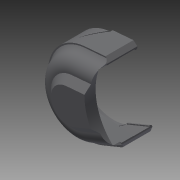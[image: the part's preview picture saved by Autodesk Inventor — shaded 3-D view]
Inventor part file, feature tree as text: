
AUTODESK INVENTOR PART (.ipt)
format: ipt  version: 2015 SP1 (Build 190203100, 203)  size: 533,504 bytes
history: native  units: in
note: dims shown in document units (in); Inventor stores cm internally (conversion verified against a paired STEP export)
features: sketch x14, projected_geometry x13, extrude x11, fillet x7, chamfer x5, plane x2, mirror x2, other x1
ambient origin geometry x8: Origin, YZ Plane, XZ Plane, XY Plane, X Axis, Y Axis, Z Axis, Center Point
bodies: Solid1 (feature_tree)
feature tree (55):
  other  "mount_sketch_alt.ipt"
  extrude  "Extrusion1"  Depth=0.3937in
  extrude  "Extrusion2"  Depth=0.625in
  extrude  "Extrusion8"  Depth=0.1575in
  extrude  "Extrusion3"  Depth=3.2677in
  chamfer  "Chamfer2"  Distance=0.1575in
  chamfer  "Chamfer5"  Distance=0.125in Angle=45.0deg
  fillet  "Fillet5"  Radius=0.0197in
  extrude  "Extrusion5"  Depth=0.125in TaperAngle=0.0deg
  extrude  "Extrusion6"  Depth=0.0197in TaperAngle=0.0deg
  extrude  "Extrusion21"  Depth=0.0295in
  extrude  "Extrusion22"  Depth=0.0295in
  chamfer  "Chamfer17"  Distance=0.0787in
  fillet  "Fillet25"  Radius=0.0394in
  fillet  "Fillet26"  Radius=0.5906in
  plane  "Work Plane6"
  mirror  "Mirror4"
  sketch  "Sketch23"  dims[d165=0.2749in d166=0.0295in]
  plane  "Work Plane5"
  extrude  "Extrusion25"  Depth=0.0394in TaperAngle=0.0deg
  chamfer  "Chamfer19"  Distance=0.0039in
  fillet  "Fillet29"  Radius=0.1969in
  fillet  "Fillet30"  Radius=0.3937in
  extrude  "Extrusion26"  Depth=0.3937in
  mirror  "Mirror6"
  extrude  "Extrusion27"  Depth=0.125in
  sketch  "Sketch28"  dims[d172=0.0197in d173=0.0394in d174=45.0deg d176=0.0394in d177=0.5906in]
  fillet  "Fillet31"  Radius=0.1969in
  chamfer  "Chamfer20"  Distance=0.0394in
  fillet  "Fillet32"  Radius=0.0394in
  sketch  "Sketch2"  dims[d0=0.3937in d1=2.507in]
  sketch  "Sketch3"  dims[d2=0.9398in d6=0.625in]
  sketch  "Sketch4"  dims[d7=0.6in d8=0.0in d9=0.1575in]
  projected_geometry  "Projected Loop1"
  sketch  "Sketch5"  dims[d10=0.52in d11=0.3in d12=0.0in d13=0.0in d18=3.2677in]
  projected_geometry  "Projected Loop2"
  sketch  "Sketch7"  dims[d19=0.9in]
  projected_geometry  "Projected Loop4"
  sketch  "Sketch8"  dims[d20=0.0394in]
  sketch  "Sketch10"  dims[d22=0.0in d23=0.1575in d24=0.0in d25=0.1181in d26=0.125in d27=45.0deg d44=0.0197in]
  projected_geometry  "Projected Loop6"
  sketch  "Sketch21"  dims[d45=0.1181in d46=0.125in d47=45.0deg d57=0.1in d58=0.0in]
  projected_geometry  "Projected Loop21"
  projected_geometry  "Projected Loop22"
  projected_geometry  "Projected Loop23"
  sketch  "Sketch22"  dims[d59=0.1in d60=0.0in d89=0.0197in d90=0.0in]
  projected_geometry  "Projected Loop24"
  projected_geometry  "Projected Loop28"
  sketch  "Sketch27"  dims[d167=0.315in d168=0.0in d169=0.0295in d170=0.0787in d171=0.0in]
  projected_geometry  "Projected Loop29"
  sketch  "Sketch30"  dims[d198=3.5827in d199=0.0394in d200=0.0in]
  projected_geometry  "Projected Loop30"
  projected_geometry  "Projected Loop31"
  sketch  "Sketch31"  dims[d201=0.0197in d202=0.0039in d203=90.0deg d204=0.1969in d205=0.0394in d206=45.0deg d208=0.3937in d209=0.3937in d210=0.0295in d211=0.1969in d213=0.0394in d214=0.0in d217=0.0394in d218=0.0in d219=0.7559in d220=0.3937in d221=0.0295in d222=0.0295in d223=0.125in d224=45.0deg d225=0.125in]
  projected_geometry  "Projected Loop33"
